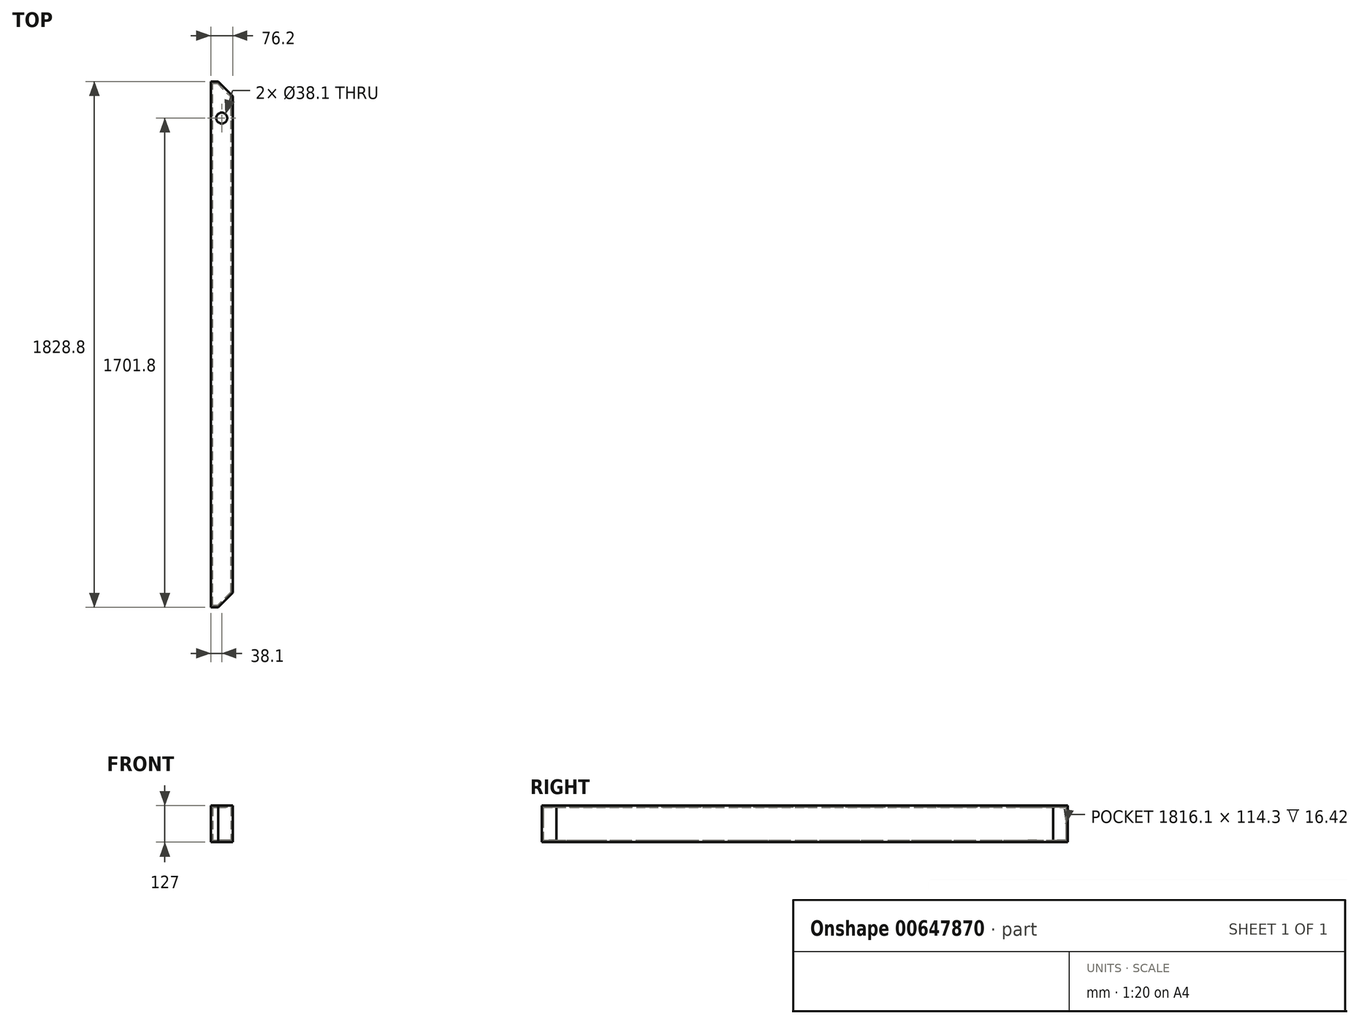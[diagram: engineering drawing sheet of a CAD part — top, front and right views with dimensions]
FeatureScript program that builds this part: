
annotation { "Feature Type Name" : "Feature", "Feature Type Description" : "" }
export const myFeature = defineFeature(function(context is Context, id is Id, definition is map)
    precondition{}
    {
        {
            var Q0;
            Q0=qCreatedBy(makeId("Front.planeOp"),FACE);
            var sketch = newSketch(context, id + "F0", { "sketchPlane" : qUnion([Q0])});
            skLineSegment(sketch, "E0.bottom", {"start": v(0, 63.5) * mm, "end": v(-76.2, 63.5) * mm});
            skLineSegment(sketch, "E0.top", {"start": v(0, -63.5) * mm, "end": v(-76.2, -63.5) * mm});
            skLineSegment(sketch, "E0.left", {"start": v(0, 63.5) * mm, "end": v(0, -63.5) * mm});
            skLineSegment(sketch, "E0.right", {"start": v(-76.2, 63.5) * mm, "end": v(-76.2, -63.5) * mm});
            skLineSegment(sketch, "E1.bottom", {"start": v(-69.85, 57.15) * mm, "end": v(-6.35, 57.15) * mm});
            skLineSegment(sketch, "E1.top", {"start": v(-69.85, -57.15) * mm, "end": v(-6.35, -57.15) * mm});
            skLineSegment(sketch, "E1.left", {"start": v(-69.85, 57.15) * mm, "end": v(-69.85, -57.15) * mm});
            skLineSegment(sketch, "E1.right", {"start": v(-6.35, 57.15) * mm, "end": v(-6.35, -57.15) * mm});
            skSolve(sketch);
        }
        {
            var Q0;
            Q0 = qSketchRegion(id + "F0", true);
            extrude(context, id + "F1", {"entities" : qUnion([Q0]), "endBound" : BoundingType.SYMMETRIC, "depth" : 1828.8 * mm, "offsetDistance" : 25.4 * mm});
        }
        {
            var Q0;
            Q0=makeQuery(id+"F1.opExtrude","SWEPT_FACE",FACE,{"disambiguationData":[OSD([sQuery(id+"F0.wireOp",EDGE,"E0.bottom")])]});
            var sketch = newSketch(context, id + "F2", { "sketchPlane" : qUnion([Q0])});
            skCircle(sketch, "E2", {"center": v(-38.1, 787.4) * mm, "radius": 19.05 * mm});
            skPoint(sketch, "E2.centerSnap0", {"position": v(-38.1, 914.4) * mm});
            skSolve(sketch);
        }
        {
            var Q0;
            Q0 = qSketchRegion(id + "F2", true);
            extrude(context, id + "F3", {"entities" : qUnion([Q0]), "operationType" : NewBodyOperationType.REMOVE, "endBound" : BoundingType.THROUGH_ALL, "oppositeDirection" : true, "depth" : 25.4 * mm, "offsetDistance" : 25.4 * mm});
        }
        {
            var Q0;
            Q0=qCreatedBy(makeId("Top.planeOp"),FACE);
            var sketch = newSketch(context, id + "F4", { "sketchPlane" : qUnion([Q0])});
            skLineSegment(sketch, "E3", {"start": v(-50.8, -914.4) * mm, "end": v(0, -863.6) * mm});
            skLineSegment(sketch, "E4", {"start": v(0, -863.6) * mm, "end": v(0, -914.4) * mm});
            skLineSegment(sketch, "E5", {"start": v(0, -914.4) * mm, "end": v(-50.8, -914.4) * mm});
            skLineSegment(sketch, "E6", {"start": v(0, 914.4) * mm, "end": v(0, 863.6) * mm});
            skLineSegment(sketch, "E7", {"start": v(0, 863.6) * mm, "end": v(-50.8, 914.4) * mm});
            skLineSegment(sketch, "E8", {"start": v(-50.8, 914.4) * mm, "end": v(0, 914.4) * mm});
            skSolve(sketch);
        }
        {
            var Q0;
            Q0 = qSketchRegion(id + "F4", true);
            var Q1;
            Q1=makeQuery(id+"F1.opExtrude","SWEPT_FACE",FACE,{"disambiguationData":[OSD([sQuery(id+"F0.wireOp",EDGE,"E0.bottom")])]});
            var Q2;
            Q2=makeQuery(id+"F1.opExtrude","SWEPT_FACE",FACE,{"disambiguationData":[OSD([sQuery(id+"F0.wireOp",EDGE,"E0.top")])]});
            extrude(context, id + "F5", {"entities" : qUnion([Q0]), "operationType" : NewBodyOperationType.REMOVE, "endBound" : BoundingType.UP_TO_SURFACE, "depth" : 25.4 * mm, "endBoundEntityFace" : qUnion([Q1]), "offsetDistance" : 25.4 * mm, "hasSecondDirection" : true, "secondDirectionBound" : SecondDirectionBoundingType.UP_TO_SURFACE, "secondDirectionOppositeDirection" : true, "secondDirectionDepth" : 25.4 * mm, "secondDirectionBoundEntityFace" : qUnion([Q2])});
        }
        {
            var Q0;
            Q0=qCreatedBy(makeId("Top.planeOp"),FACE);
            var sketch = newSketch(context, id + "F6", { "sketchPlane" : qUnion([Q0])});
            skLineSegment(sketch, "E9", {"start": v(-76.2, -914.4) * mm, "end": v(-50.8, -914.4) * mm});
            skLineSegment(sketch, "E10", {"start": v(-50.8, -914.4) * mm, "end": v(0, -863.6) * mm});
            skLineSegment(sketch, "E11", {"start": v(-76.2, -914.4) * mm, "end": v(-76.2, -908.05) * mm});
            skLineSegment(sketch, "E12", {"start": v(-76.2, -908.05) * mm, "end": v(-53.43, -908.05) * mm});
            skLineSegment(sketch, "E13", {"start": v(-53.43, -908.05) * mm, "end": v(0, -854.62) * mm});
            skLineSegment(sketch, "E14", {"start": v(0, -854.62) * mm, "end": v(0, -863.6) * mm});
            skSolve(sketch);
        }
        {
            var Q0;
            Q0 = qSketchRegion(id + "F6", true);
            var Q1;
            Q1=makeQuery(id+"F1.opExtrude","SWEPT_FACE",FACE,{"disambiguationData":[OSD([sQuery(id+"F0.wireOp",EDGE,"E0.bottom")])]});
            var Q2;
            Q2=makeQuery(id+"F1.opExtrude","SWEPT_FACE",FACE,{"disambiguationData":[OSD([sQuery(id+"F0.wireOp",EDGE,"E0.top")])]});
            extrude(context, id + "F7", {"entities" : qUnion([Q0]), "operationType" : NewBodyOperationType.ADD, "endBound" : BoundingType.UP_TO_SURFACE, "depth" : 25.4 * mm, "endBoundEntityFace" : qUnion([Q1]), "offsetDistance" : 25.4 * mm, "hasSecondDirection" : true, "secondDirectionBound" : SecondDirectionBoundingType.UP_TO_SURFACE, "secondDirectionOppositeDirection" : true, "secondDirectionDepth" : 25.4 * mm, "secondDirectionBoundEntityFace" : qUnion([Q2])});
        }
        {
            var Q0;
            Q0=qCreatedBy(makeId("Top.planeOp"),FACE);
            var sketch = newSketch(context, id + "F8", { "sketchPlane" : qUnion([Q0])});
            skLineSegment(sketch, "E15", {"start": v(-76.2, 914.4) * mm, "end": v(-50.8, 914.4) * mm});
            skLineSegment(sketch, "E16", {"start": v(-50.8, 914.4) * mm, "end": v(0, 863.6) * mm});
            skLineSegment(sketch, "E17", {"start": v(0, 863.6) * mm, "end": v(0, 854.62) * mm});
            skLineSegment(sketch, "E18", {"start": v(0, 854.62) * mm, "end": v(-53.43, 908.05) * mm});
            skLineSegment(sketch, "E19", {"start": v(-53.43, 908.05) * mm, "end": v(-76.2, 908.05) * mm});
            skLineSegment(sketch, "E20", {"start": v(-76.2, 908.05) * mm, "end": v(-76.2, 914.4) * mm});
            skSolve(sketch);
        }
        {
            var Q0;
            Q0 = qSketchRegion(id + "F8", true);
            var Q1;
            Q1=makeQuery(id+"F1.opExtrude","SWEPT_FACE",FACE,{"disambiguationData":[OSD([sQuery(id+"F0.wireOp",EDGE,"E0.bottom")])]});
            var Q2;
            Q2=makeQuery(id+"F1.opExtrude","SWEPT_FACE",FACE,{"disambiguationData":[OSD([sQuery(id+"F0.wireOp",EDGE,"E0.top")])]});
            extrude(context, id + "F9", {"entities" : qUnion([Q0]), "operationType" : NewBodyOperationType.ADD, "endBound" : BoundingType.UP_TO_SURFACE, "depth" : 25.4 * mm, "endBoundEntityFace" : qUnion([Q1]), "offsetDistance" : 25.4 * mm, "hasSecondDirection" : true, "secondDirectionBound" : SecondDirectionBoundingType.UP_TO_SURFACE, "secondDirectionOppositeDirection" : true, "secondDirectionDepth" : 25.4 * mm, "secondDirectionBoundEntityFace" : qUnion([Q2])});
        }
    });
